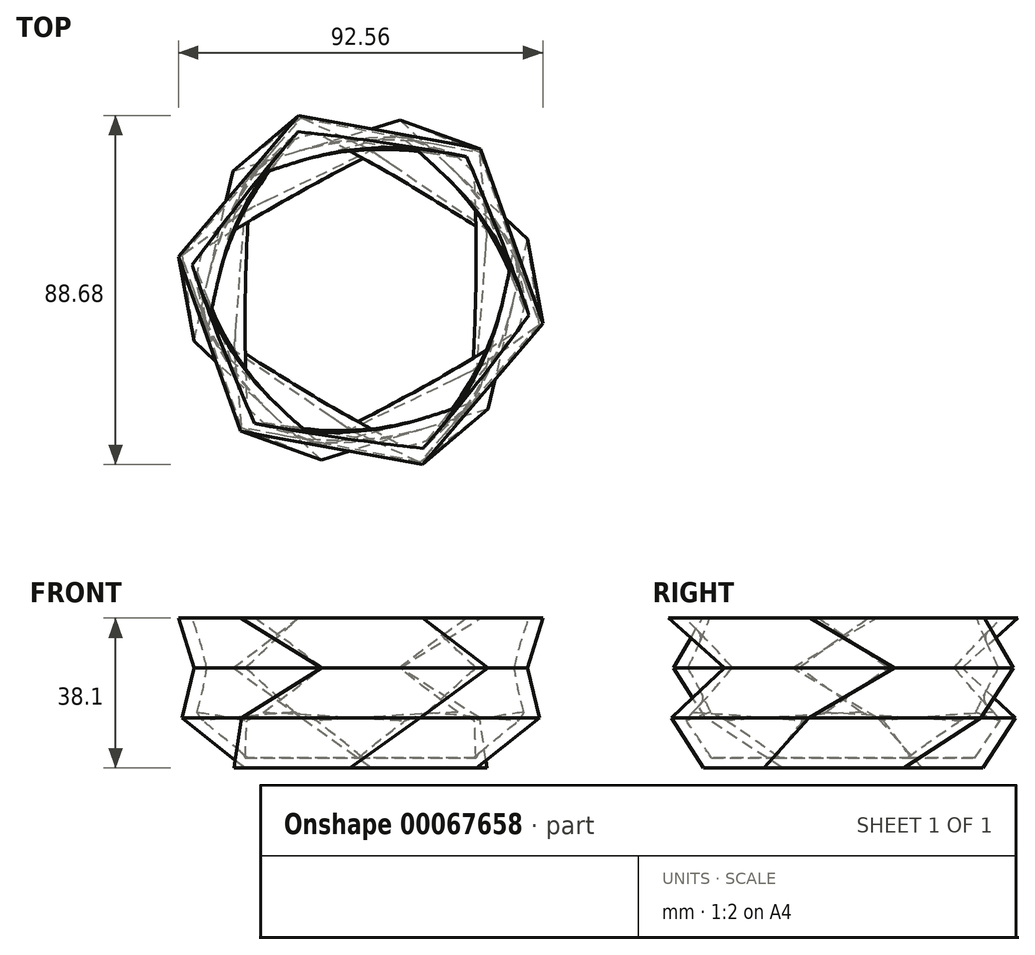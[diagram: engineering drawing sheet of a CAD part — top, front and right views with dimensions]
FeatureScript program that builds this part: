
annotation { "Feature Type Name" : "Feature", "Feature Type Description" : "" }
export const myFeature = defineFeature(function(context is Context, id is Id, definition is map)
    precondition{}
    {
        {
            var Q0;
            Q0=qCreatedBy(makeId("Top.planeOp"),FACE);
            cPlane(context, id + "F0", {"entities" : qUnion([Q0]), "cplaneType" : CPlaneType.OFFSET, "offset" : 12.7 * mm, "width" : 152.4 * mm, "height" : 152.4 * mm});
        }
        {
            var Q0;
            Q0=qCreatedBy(makeId("Top.planeOp"),FACE);
            var sketch = newSketch(context, id + "F1", { "sketchPlane" : qUnion([Q0])});
            skCircle(sketch, "E0.cCircle", {"center": v(0, 0) * mm, "radius": 35.62 * mm, "construction": true});
            skLineSegment(sketch, "E0.0", {"start": v(-29.4, 20.1) * mm, "end": v(2.7, 35.52) * mm});
            skLineSegment(sketch, "E0.1", {"start": v(2.7, 35.52) * mm, "end": v(32.12, 15.42) * mm});
            skLineSegment(sketch, "E0.2", {"start": v(32.12, 15.42) * mm, "end": v(29.4, -20.1) * mm});
            skLineSegment(sketch, "E0.3", {"start": v(29.4, -20.1) * mm, "end": v(-2.7, -35.52) * mm});
            skLineSegment(sketch, "E0.4", {"start": v(-2.7, -35.52) * mm, "end": v(-32.12, -15.42) * mm});
            skLineSegment(sketch, "E0.5", {"start": v(-32.12, -15.42) * mm, "end": v(-29.4, 20.1) * mm});
            skSolve(sketch);
        }
        {
            var Q0;
            Q0 = qSketchRegion(id + "F1", true);
            var sketch = newSketch(context, id + "F2", { "sketchPlane" : qUnion([Q0])});
            skSolve(sketch);
        }
        {
            var Q0;
            Q0=qCreatedBy(id+"F0.planeOp",FACE);
            var sketch = newSketch(context, id + "F3", { "sketchPlane" : qUnion([Q0])});
            skCircle(sketch, "E1.cCircle", {"center": v(0, 0) * mm, "radius": 46.24 * mm, "construction": true});
            skLineSegment(sketch, "E1.0", {"start": v(-15.12, 43.7) * mm, "end": v(30.28, 34.94) * mm});
            skLineSegment(sketch, "E1.1", {"start": v(30.28, 34.94) * mm, "end": v(45.4, -8.75) * mm});
            skLineSegment(sketch, "E1.2", {"start": v(45.4, -8.75) * mm, "end": v(15.12, -43.7) * mm});
            skLineSegment(sketch, "E1.3", {"start": v(15.12, -43.7) * mm, "end": v(-30.28, -34.94) * mm});
            skLineSegment(sketch, "E1.4", {"start": v(-30.28, -34.94) * mm, "end": v(-45.4, 8.75) * mm});
            skLineSegment(sketch, "E1.5", {"start": v(-45.4, 8.75) * mm, "end": v(-15.12, 43.7) * mm});
            skSolve(sketch);
        }
        {
            var Q0;
            Q0=makeQuery(id+"F2.imprint","IMPRINT",FACE,{"disambiguationData":[TD([[makeQuery(id+"F2.imprint","IMPRINT",EDGE,{"derivedFrom":makeQuery(id+"F1.imprint","IMPRINT",EDGE,{"derivedFrom":sQuery(id+"F1.wireOp",EDGE,"E0.0")})}),-1.0]])]});
            var Q1;
            Q1=makeQuery(id+"F3.imprint","IMPRINT",FACE,{"disambiguationData":[TD([[makeQuery(id+"F3.imprint","IMPRINT",EDGE,{"derivedFrom":sQuery(id+"F3.wireOp",EDGE,"E1.0")}),-1.0]])]});
            loft(context, id + "F4", {"sheetProfilesArray" : [{ "sheetProfileEntities" : qUnion([Q0]) }, { "sheetProfileEntities" : qUnion([Q1]) }]});
        }
        {
            var Q0;
            Q0=qCreatedBy(id+"F0.planeOp",FACE);
            cPlane(context, id + "F5", {"entities" : qUnion([Q0]), "cplaneType" : CPlaneType.OFFSET, "offset" : 12.7 * mm, "width" : 152.4 * mm, "height" : 152.4 * mm});
        }
        {
            var Q0;
            Q0=qCreatedBy(id+"F5.planeOp",FACE);
            var sketch = newSketch(context, id + "F6", { "sketchPlane" : qUnion([Q0])});
            skCircle(sketch, "E2.cCircle", {"center": v(0, 0) * mm, "radius": 44.3 * mm, "construction": true});
            skLineSegment(sketch, "E2.0", {"start": v(-42.37, -12.96) * mm, "end": v(-32.4, 30.21) * mm});
            skLineSegment(sketch, "E2.1", {"start": v(-32.4, 30.21) * mm, "end": v(9.96, 43.17) * mm});
            skLineSegment(sketch, "E2.2", {"start": v(9.96, 43.17) * mm, "end": v(42.37, 12.96) * mm});
            skLineSegment(sketch, "E2.3", {"start": v(42.37, 12.96) * mm, "end": v(32.4, -30.21) * mm});
            skLineSegment(sketch, "E2.4", {"start": v(32.4, -30.21) * mm, "end": v(-9.96, -43.17) * mm});
            skLineSegment(sketch, "E2.5", {"start": v(-9.96, -43.17) * mm, "end": v(-42.37, -12.96) * mm});
            skSolve(sketch);
        }
        {
            var Q1;
            Q1=makeQuery(id+"F4.opLoft","CAP_FACE",FACE,{"disambiguationData":[OSD([makeQuery(id+"F3.imprint","IMPRINT",FACE,{"disambiguationData":[TD([[makeQuery(id+"F3.imprint","IMPRINT",EDGE,{"derivedFrom":sQuery(id+"F3.wireOp",EDGE,"E1.0")}),-1.0]])]})])],"isStart":true});
            var Q2;
            Q2=makeQuery(id+"F6.imprint","IMPRINT",FACE,{"disambiguationData":[TD([[makeQuery(id+"F6.imprint","IMPRINT",EDGE,{"derivedFrom":sQuery(id+"F6.wireOp",EDGE,"E2.0")}),-1.0]])]});
            loft(context, id + "F7", {"operationType" : NewBodyOperationType.ADD, "sheetProfilesArray" : [{ "sheetProfileEntities" : qUnion([Q1]) }, { "sheetProfileEntities" : qUnion([Q2]) }]});
        }
        {
            var Q0;
            Q0=qCreatedBy(id+"F5.planeOp",FACE);
            cPlane(context, id + "F8", {"entities" : qUnion([Q0]), "cplaneType" : CPlaneType.OFFSET, "offset" : 12.7 * mm, "width" : 152.4 * mm, "height" : 152.4 * mm});
        }
        {
            var Q0;
            Q0=qCreatedBy(id+"F8.planeOp",FACE);
            var sketch = newSketch(context, id + "F9", { "sketchPlane" : qUnion([Q0])});
            skCircle(sketch, "E3.cCircle", {"center": v(0, 0) * mm, "radius": 47.06 * mm, "construction": true});
            skLineSegment(sketch, "E3.0", {"start": v(-30.52, -35.82) * mm, "end": v(-46.28, 8.53) * mm});
            skLineSegment(sketch, "E3.1", {"start": v(-46.28, 8.53) * mm, "end": v(-15.75, 44.34) * mm});
            skLineSegment(sketch, "E3.2", {"start": v(-15.75, 44.34) * mm, "end": v(30.52, 35.82) * mm});
            skLineSegment(sketch, "E3.3", {"start": v(30.52, 35.82) * mm, "end": v(46.28, -8.53) * mm});
            skLineSegment(sketch, "E3.4", {"start": v(46.28, -8.53) * mm, "end": v(15.75, -44.34) * mm});
            skLineSegment(sketch, "E3.5", {"start": v(15.75, -44.34) * mm, "end": v(-30.52, -35.82) * mm});
            skSolve(sketch);
        }
        {
            var Q1;
            Q1=makeQuery(id+"F7.opLoft","CAP_FACE",FACE,{"disambiguationData":[OSD([makeQuery(id+"F6.imprint","IMPRINT",FACE,{"disambiguationData":[TD([[makeQuery(id+"F6.imprint","IMPRINT",EDGE,{"derivedFrom":sQuery(id+"F6.wireOp",EDGE,"E2.0")}),-1.0]])]})])],"isStart":true});
            var Q2;
            Q2=makeQuery(id+"F9.imprint","IMPRINT",FACE,{"disambiguationData":[TD([[makeQuery(id+"F9.imprint","IMPRINT",EDGE,{"derivedFrom":sQuery(id+"F9.wireOp",EDGE,"E3.0")}),-1.0]])]});
            loft(context, id + "F10", {"operationType" : NewBodyOperationType.ADD, "sheetProfilesArray" : [{ "sheetProfileEntities" : qUnion([Q1]) }, { "sheetProfileEntities" : qUnion([Q2]) }]});
        }
        {
            var Q0;
            Q0=makeQuery(id+"F10.opLoft","CAP_FACE",FACE,{"disambiguationData":[OSD([makeQuery(id+"F9.imprint","IMPRINT",FACE,{"disambiguationData":[TD([[makeQuery(id+"F9.imprint","IMPRINT",EDGE,{"derivedFrom":sQuery(id+"F9.wireOp",EDGE,"E3.0")}),-1.0]])]})])],"isStart":true});
            shell(context, id + "F11", {"entities" : qUnion([Q0]), "thickness" : 2.54 * mm});
        }
    });
